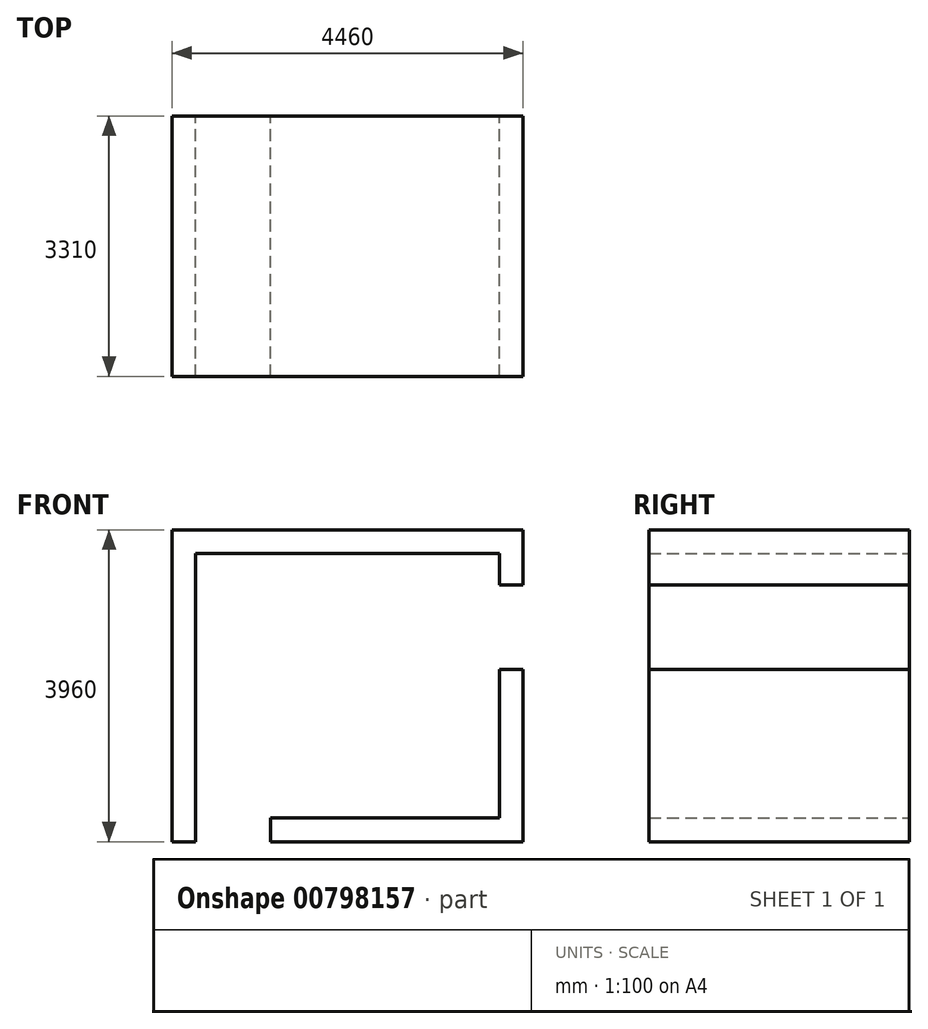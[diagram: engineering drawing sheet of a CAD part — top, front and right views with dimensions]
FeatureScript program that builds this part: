
annotation { "Feature Type Name" : "Feature", "Feature Type Description" : "" }
export const myFeature = defineFeature(function(context is Context, id is Id, definition is map)
    precondition{}
    {
        {
            var Q0;
            Q0=qCreatedBy(makeId("Front.planeOp"),FACE);
            var sketch = newSketch(context, id + "F0", { "sketchPlane" : qUnion([Q0])});
            skLineSegment(sketch, "E0", {"start": v(0, 0) * mm, "end": v(3860, 0) * mm});
            skLineSegment(sketch, "E1", {"start": v(0, 0) * mm, "end": v(0, -3360) * mm});
            skLineSegment(sketch, "E2", {"start": v(950, -3360) * mm, "end": v(3860, -3360) * mm});
            skLineSegment(sketch, "E3", {"start": v(3860, -3360) * mm, "end": v(3860, -1470) * mm});
            skLineSegment(sketch, "E4.0", {"start": v(-300, 300) * mm, "end": v(4160, 300) * mm});
            skLineSegment(sketch, "E4.1", {"start": v(-300, 300) * mm, "end": v(-300, -3660) * mm});
            skLineSegment(sketch, "E4.2", {"start": v(-300, -3660) * mm, "end": v(0, -3660) * mm});
            skLineSegment(sketch, "E4.3", {"start": v(4160, -3660) * mm, "end": v(4160, -1470) * mm});
            skLineSegment(sketch, "E5", {"start": v(950, -3360) * mm, "end": v(950, -3660) * mm});
            skLineSegment(sketch, "E6", {"start": v(0, -3360) * mm, "end": v(0, -3660) * mm});
            skLineSegment(sketch, "E7.trimOffspring", {"start": v(950, -3660) * mm, "end": v(4160, -3660) * mm});
            skLineSegment(sketch, "E8", {"start": v(3860, -400) * mm, "end": v(4160, -400) * mm});
            skLineSegment(sketch, "E9", {"start": v(3860, -1470) * mm, "end": v(4160, -1470) * mm});
            skLineSegment(sketch, "E10.trimOffspring", {"start": v(3860, -400) * mm, "end": v(3860, 0) * mm});
            skLineSegment(sketch, "E11.trimOffspring", {"start": v(4160, -400) * mm, "end": v(4160, 300) * mm});
            skSolve(sketch);
        }
        {
            var Q0;
            Q0=makeQuery(id+"F0.imprint","IMPRINT",FACE,{"disambiguationData":[TD([[makeQuery(id+"F0.imprint","IMPRINT",EDGE,{"derivedFrom":sQuery(id+"F0.wireOp",EDGE,"E0")}),1.0]])]});
            var Q1;
            Q1=makeQuery(id+"F0.imprint","IMPRINT",FACE,{"disambiguationData":[TD([[makeQuery(id+"F0.imprint","IMPRINT",EDGE,{"derivedFrom":sQuery(id+"F0.wireOp",EDGE,"E2")}),-1.0]])]});
            extrude(context, id + "F1", {"entities" : qUnion([Q0, Q1]), "depth" : 3310 * mm, "offsetDistance" : 25 * mm});
        }
    });
